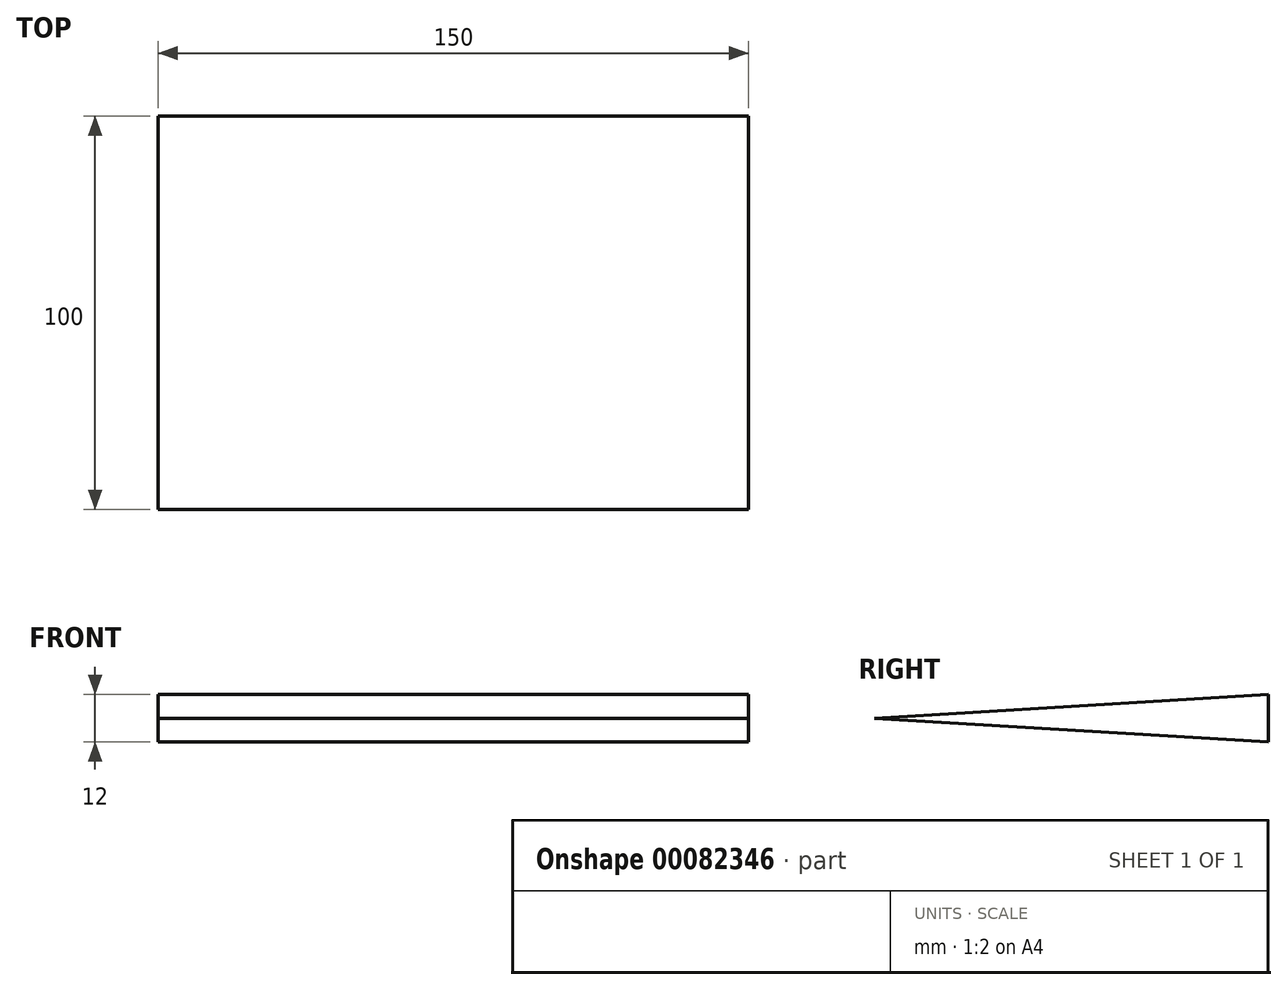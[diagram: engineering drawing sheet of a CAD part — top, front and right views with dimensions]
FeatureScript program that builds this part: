
annotation { "Feature Type Name" : "Feature", "Feature Type Description" : "" }
export const myFeature = defineFeature(function(context is Context, id is Id, definition is map)
    precondition{}
    {
        {
            var Q0;
            Q0=qCreatedBy(makeId("Top.planeOp"),FACE);
            var sketch = newSketch(context, id + "F0", { "sketchPlane" : qUnion([Q0])});
            skLineSegment(sketch, "E0.bottom", {"start": v(0, 0) * mm, "end": v(-150, 0) * mm});
            skLineSegment(sketch, "E0.top", {"start": v(0, 100) * mm, "end": v(-150, 100) * mm});
            skLineSegment(sketch, "E0.left", {"start": v(0, 0) * mm, "end": v(0, 100) * mm});
            skLineSegment(sketch, "E0.right", {"start": v(-150, 0) * mm, "end": v(-150, 100) * mm});
            skSolve(sketch);
        }
        {
            var Q0;
            Q0=makeQuery(id+"F0.imprint","IMPRINT",FACE,{"disambiguationData":[TD([[makeQuery(id+"F0.imprint","IMPRINT",EDGE,{"derivedFrom":sQuery(id+"F0.wireOp",EDGE,"E0.bottom")}),-1.0]])]});
            extrude(context, id + "F1", {"entities" : qUnion([Q0]), "depth" : 12 * mm});
        }
        {
            var Q0;
            Q0=makeQuery(id+"F1.opExtrude","CAP_EDGE",EDGE,{"disambiguationData":[OSD([sQuery(id+"F0.wireOp",EDGE,"E0.bottom")])],"isStart":false});
            var Q1;
            Q1=makeQuery(id+"F1.opExtrude","CAP_EDGE",EDGE,{"disambiguationData":[OSD([sQuery(id+"F0.wireOp",EDGE,"E0.bottom")])],"isStart":true});
            chamfer(context, id + "F2", {"entities" : qUnion([Q0, Q1]), "chamferType" : ChamferType.TWO_OFFSETS, "width1" : 6 * mm, "oppositeDirection" : false, "width2" : 100 * mm, "tangentPropagation" : true});
        }
    });
